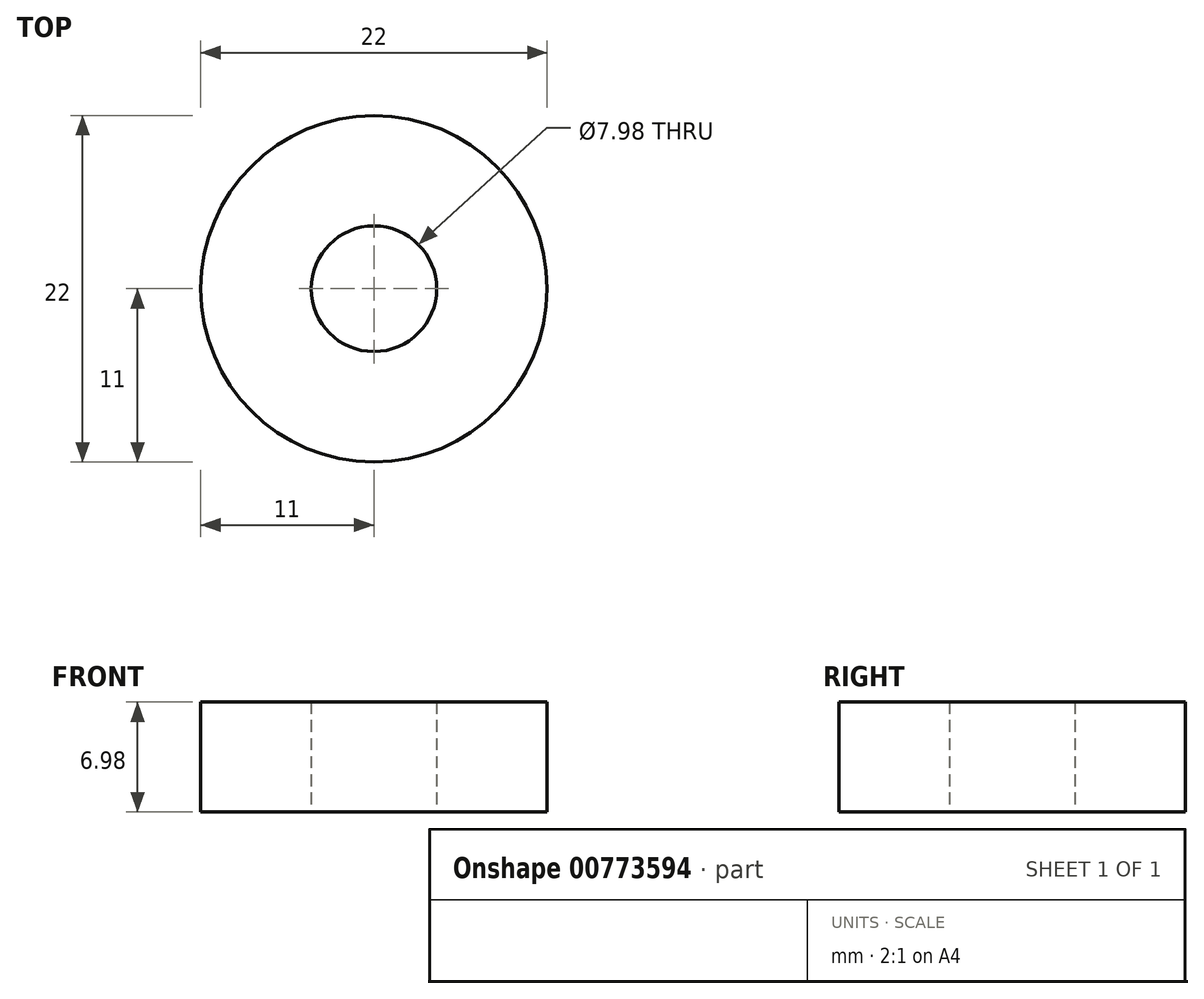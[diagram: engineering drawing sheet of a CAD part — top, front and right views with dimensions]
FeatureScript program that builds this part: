
annotation { "Feature Type Name" : "Feature", "Feature Type Description" : "" }
export const myFeature = defineFeature(function(context is Context, id is Id, definition is map)
    precondition{}
    {
        {
            var Q0;
            Q0=qCreatedBy(makeId("Top.planeOp"),FACE);
            var sketch = newSketch(context, id + "F0", { "sketchPlane" : qUnion([Q0])});
            skCircle(sketch, "E0", {"center": v(0, 0) * mm, "radius": 11 * mm});
            skCircle(sketch, "E1", {"center": v(0, 0) * mm, "radius": 3.99 * mm});
            skSolve(sketch);
        }
        {
            var Q0;
            Q0 = qSketchRegion(id + "F0", true);
            extrude(context, id + "F1", {"entities" : qUnion([Q0]), "endBound" : BoundingType.SYMMETRIC, "depth" : 7 * mm, "offsetDistance" : 25.4 * mm});
        }
    });
